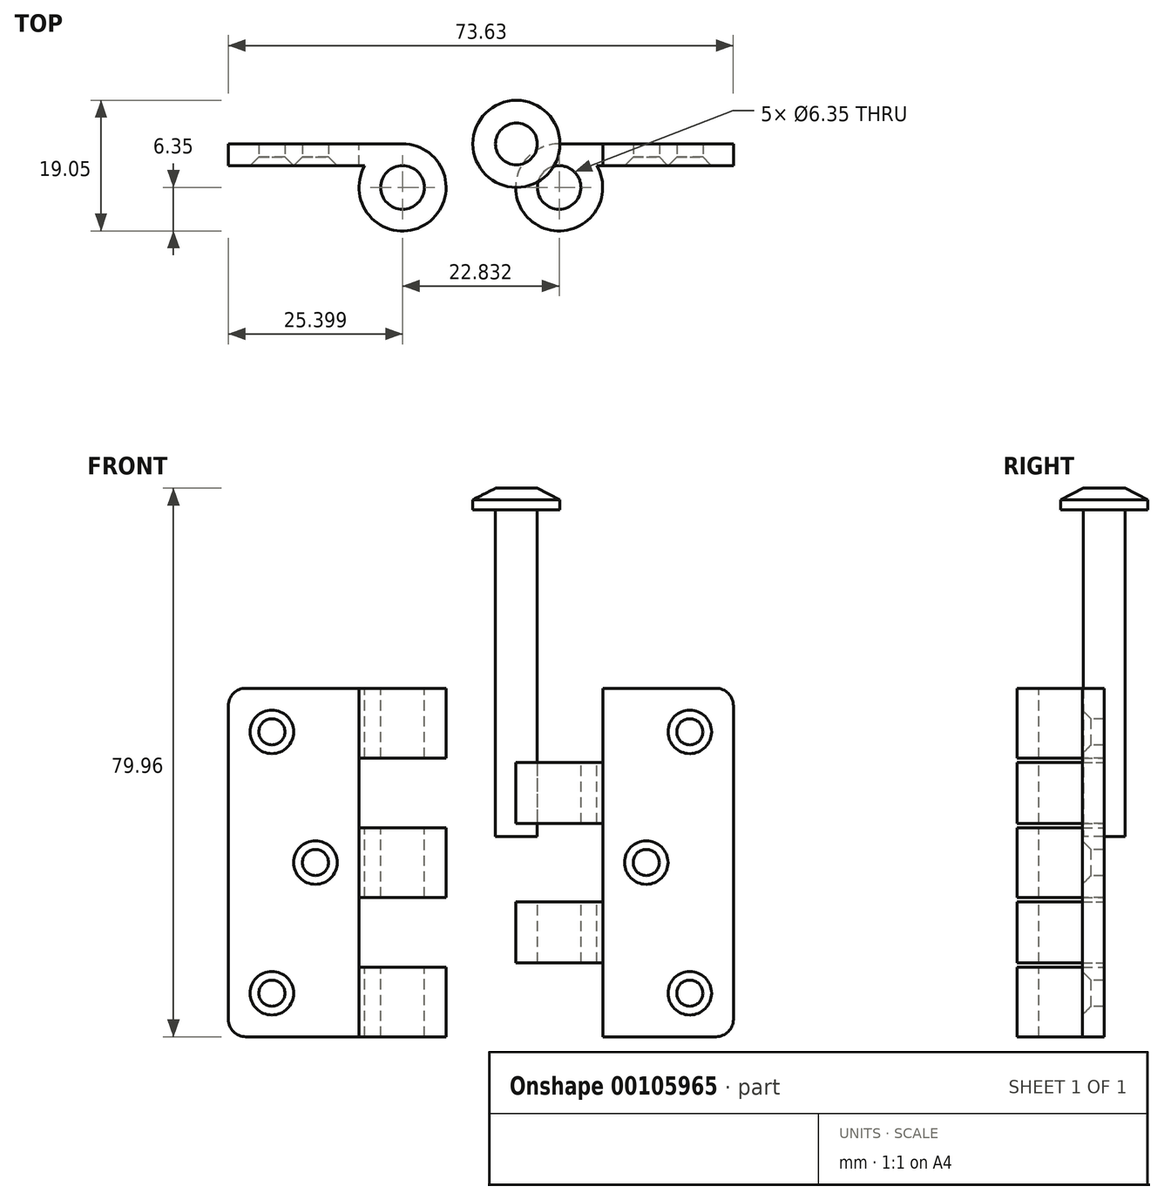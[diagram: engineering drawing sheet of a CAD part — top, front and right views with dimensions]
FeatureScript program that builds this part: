
annotation { "Feature Type Name" : "Feature", "Feature Type Description" : "" }
export const myFeature = defineFeature(function(context is Context, id is Id, definition is map)
    precondition{}
    {
        {
            var Q0;
            Q0=qCreatedBy(makeId("Front.planeOp"),FACE);
            var sketch = newSketch(context, id + "F0", { "sketchPlane" : qUnion([Q0])});
            skLineSegment(sketch, "E0.bottom", {"start": v(-44.61, 38.03) * mm, "end": v(-19.21, 38.03) * mm});
            skLineSegment(sketch, "E0.top", {"start": v(-44.61, -12.77) * mm, "end": v(-19.21, -12.77) * mm});
            skLineSegment(sketch, "E0.left", {"start": v(-44.61, 38.03) * mm, "end": v(-44.61, -12.77) * mm});
            skLineSegment(sketch, "E0.right", {"start": v(-19.21, 38.03) * mm, "end": v(-19.21, -12.77) * mm});
            skSolve(sketch);
        }
        {
            var Q0;
            Q0 = qSketchRegion(id + "F0", true);
            extrude(context, id + "F1", {"entities" : qUnion([Q0]), "depth" : 3.17 * mm});
        }
        {
            var Q0;
            Q0=makeQuery(id+"F1.opExtrude","SWEPT_FACE",FACE,{"disambiguationData":[OSD([sQuery(id+"F0.wireOp",EDGE,"E0.bottom")])]});
            var sketch = newSketch(context, id + "F2", { "sketchPlane" : qUnion([Q0])});
            skCircle(sketch, "E1", {"center": v(-19.21, -6.35) * mm, "radius": 6.35 * mm});
            skCircle(sketch, "E2", {"center": v(-19.21, -6.35) * mm, "radius": 3.18 * mm});
            skSolve(sketch);
        }
        {
            var Q0;
            {var subQ5=sQuery(id+"F2.wireOp",EDGE,"E2");Q0=makeQuery(id+"F2.imprint","IMPRINT",FACE,{"disambiguationData":[TD([[makeQuery(id+"F2.imprint","IMPRINT",EDGE,{"derivedFrom":subQ5}),-1.0]])]});}
            var Q1;
            {var subQ1=sQuery(id+"F0.wireOp",EDGE,"E0.bottom");var subQ2=makeQuery(id+"F1.opExtrude","SWEPT_EDGE",EDGE,{"disambiguationData":[OSD([subQ1,sQuery(id+"F0.wireOp",EDGE,"E0.right")])]});Q1=makeQuery(id+"F2.imprint","IMPRINT",FACE,{"disambiguationData":[TD([[makeQuery(id+"F2.imprint","IMPRINT",EDGE,{"derivedFrom":subQ2}),1.0]])]});}
            var Q2;
            Q2=makeQuery(id+"F1.opExtrude","SWEPT_FACE",FACE,{"disambiguationData":[OSD([sQuery(id+"F0.wireOp",EDGE,"E0.top")])]});
            extrude(context, id + "F3", {"entities" : qUnion([Q0, Q1]), "operationType" : NewBodyOperationType.ADD, "endBound" : BoundingType.UP_TO_SURFACE, "oppositeDirection" : true, "endBoundEntityFace" : qUnion([Q2]), "depth" : 25.4 * mm});
        }
        {
            var Q0;
            Q0=makeQuery(id+"F1.opExtrude","CAP_FACE",FACE,{"disambiguationData":[OSD([sQuery(id+"F0.wireOp",EDGE,"E0.bottom"),sQuery(id+"F0.wireOp",EDGE,"E0.top"),sQuery(id+"F0.wireOp",EDGE,"E0.left"),sQuery(id+"F0.wireOp",EDGE,"E0.right")])],"isStart":false});
            var sketch = newSketch(context, id + "F4", { "sketchPlane" : qUnion([Q0])});
            skLineSegment(sketch, "E3", {"start": v(-34.66, 38.03) * mm, "end": v(-34.66, -12.77) * mm, "construction": true});
            skLineSegment(sketch, "E4", {"start": v(-24.7, 12.63) * mm, "end": v(-44.61, 12.63) * mm, "construction": true});
            skLineSegment(sketch, "E5", {"start": v(-24.7, -6.42) * mm, "end": v(-44.61, -6.42) * mm, "construction": true});
            skLineSegment(sketch, "E6", {"start": v(-24.7, 31.68) * mm, "end": v(-44.61, 31.68) * mm, "construction": true});
            skPoint(sketch, "E7", {"position": v(-38.26, 31.68) * mm});
            skPoint(sketch, "E8", {"position": v(-31.91, 12.63) * mm});
            skPoint(sketch, "E9", {"position": v(-38.26, -6.42) * mm});
            skSolve(sketch);
        }
        {
            var Q0;
            Q0=makeQuery(id+"F1.opExtrude","SWEPT_EDGE",EDGE,{"disambiguationData":[OSD([sQuery(id+"F0.wireOp",EDGE,"E0.bottom"),sQuery(id+"F0.wireOp",EDGE,"E0.left")])]});
            var Q1;
            Q1=makeQuery(id+"F1.opExtrude","SWEPT_EDGE",EDGE,{"disambiguationData":[OSD([sQuery(id+"F0.wireOp",EDGE,"E0.top"),sQuery(id+"F0.wireOp",EDGE,"E0.left")])]});
            fillet(context, id + "F5", {"entities" : qUnion([Q0, Q1]), "radius" : 2.54 * mm, "tangentPropagation" : true, "allowEdgeOverflow" : false});
        }
        {
            var Q0;
            Q0=makeQuery(id+"F0.imprint","IMPRINT",FACE,{"disambiguationData":[TD([[makeQuery(id+"F0.imprint","IMPRINT",EDGE,{"derivedFrom":sQuery(id+"F0.wireOp",EDGE,"E0.bottom")}),-1.0]])]});
            var sketch = newSketch(context, id + "F6", { "sketchPlane" : qUnion([Q0])});
            skLineSegment(sketch, "E10", {"start": v(-25.56, -2.61) * mm, "end": v(-12.86, -2.61) * mm});
            skLineSegment(sketch, "E11", {"start": v(-12.86, -2.61) * mm, "end": v(-12.86, 7.55) * mm});
            skLineSegment(sketch, "E12", {"start": v(-12.86, 7.55) * mm, "end": v(-25.56, 7.55) * mm});
            skLineSegment(sketch, "E13", {"start": v(-25.56, 7.55) * mm, "end": v(-25.56, -2.61) * mm});
            skLineSegment(sketch, "E14", {"start": v(-25.56, 17.7) * mm, "end": v(-12.86, 17.7) * mm});
            skLineSegment(sketch, "E15", {"start": v(-12.86, 17.7) * mm, "end": v(-12.86, 27.87) * mm});
            skLineSegment(sketch, "E16", {"start": v(-12.86, 27.87) * mm, "end": v(-25.56, 27.87) * mm});
            skLineSegment(sketch, "E17", {"start": v(-25.56, 27.87) * mm, "end": v(-25.56, 17.7) * mm});
            skPoint(sketch, "E18", {"position": v(-19.21, -2.61) * mm});
            skLineSegment(sketch, "E19", {"start": v(-19.21, 27.87) * mm, "end": v(-19.21, 38.03) * mm});
            skLineSegment(sketch, "E20", {"start": v(-19.21, 17.7) * mm, "end": v(-19.21, 7.55) * mm});
            skLineSegment(sketch, "E21", {"start": v(-19.21, -2.61) * mm, "end": v(-19.21, -12.77) * mm});
            skLineSegment(sketch, "E22", {"start": v(-12.86, 17.7) * mm, "end": v(-12.86, 7.55) * mm});
            skLineSegment(sketch, "E23", {"start": v(-25.56, 7.55) * mm, "end": v(-25.56, 17.7) * mm});
            skLineSegment(sketch, "E24", {"start": v(-25.56, 27.87) * mm, "end": v(-25.56, 38.04) * mm});
            skLineSegment(sketch, "E25", {"start": v(-25.56, 38.04) * mm, "end": v(-12.86, 38.03) * mm});
            skLineSegment(sketch, "E26", {"start": v(-12.86, 38.03) * mm, "end": v(-12.86, 27.87) * mm});
            skLineSegment(sketch, "E27", {"start": v(-12.86, -2.61) * mm, "end": v(-12.86, -12.77) * mm});
            skLineSegment(sketch, "E28", {"start": v(-12.86, -12.77) * mm, "end": v(-25.56, -12.77) * mm});
            skLineSegment(sketch, "E29", {"start": v(-25.56, -12.77) * mm, "end": v(-25.56, -2.61) * mm});
            skSolve(sketch);
        }
        {
            var Q0;
            {var subQ0=sQuery(id+"F6.wireOp",EDGE,"E17");Q0=makeQuery(id+"F6.imprint","IMPRINT",FACE,{"disambiguationData":[TD([[makeQuery(id+"F6.imprint","IMPRINT",EDGE,{"derivedFrom":subQ0}),1.0]])]});}
            var Q1;
            {var subQ0=sQuery(id+"F6.wireOp",EDGE,"E15");Q1=makeQuery(id+"F6.imprint","IMPRINT",FACE,{"disambiguationData":[TD([[makeQuery(id+"F6.imprint","IMPRINT",EDGE,{"derivedFrom":subQ0}),1.0]])]});}
            var Q2;
            {var subQ0=sQuery(id+"F6.wireOp",EDGE,"E13");Q2=makeQuery(id+"F6.imprint","IMPRINT",FACE,{"disambiguationData":[TD([[makeQuery(id+"F6.imprint","IMPRINT",EDGE,{"derivedFrom":subQ0}),1.0]])]});}
            var Q3;
            {var subQ0=sQuery(id+"F6.wireOp",EDGE,"E11");Q3=makeQuery(id+"F6.imprint","IMPRINT",FACE,{"disambiguationData":[TD([[makeQuery(id+"F6.imprint","IMPRINT",EDGE,{"derivedFrom":subQ0}),1.0]])]});}
            extrude(context, id + "F7", {"entities" : qUnion([Q0, Q1, Q2, Q3]), "operationType" : NewBodyOperationType.REMOVE, "depth" : 25.4 * mm});
        }
        {
            var Q0;
            Q0=qCreatedBy(makeId("Front.planeOp"),FACE);
            var sketch = newSketch(context, id + "F8", { "sketchPlane" : qUnion([Q0])});
            skLineSegment(sketch, "E30.bottom", {"start": v(3.62, 38.03) * mm, "end": v(29.02, 38.03) * mm});
            skLineSegment(sketch, "E30.top", {"start": v(3.62, -12.77) * mm, "end": v(29.02, -12.77) * mm});
            skLineSegment(sketch, "E30.left", {"start": v(3.62, 38.03) * mm, "end": v(3.62, -12.77) * mm});
            skLineSegment(sketch, "E30.right", {"start": v(29.02, 38.03) * mm, "end": v(29.02, -12.77) * mm});
            skSolve(sketch);
        }
        {
            var Q0;
            Q0 = qSketchRegion(id + "F8", true);
            extrude(context, id + "F9", {"entities" : qUnion([Q0]), "depth" : 3.17 * mm});
        }
        {
            var Q0;
            Q0=makeQuery(id+"F9.opExtrude","SWEPT_FACE",FACE,{"disambiguationData":[OSD([sQuery(id+"F8.wireOp",EDGE,"E30.bottom")])]});
            var sketch = newSketch(context, id + "F10", { "sketchPlane" : qUnion([Q0])});
            skCircle(sketch, "E31", {"center": v(3.62, -6.35) * mm, "radius": 6.35 * mm});
            skLineSegment(sketch, "E32", {"start": v(-33.9, -6.35) * mm, "end": v(23.07, -6.35) * mm, "construction": true});
            skCircle(sketch, "E33", {"center": v(3.62, -6.35) * mm, "radius": 3.18 * mm});
            skSolve(sketch);
        }
        {
            var Q0;
            {var subQ5=sQuery(id+"F10.wireOp",EDGE,"E33");Q0=makeQuery(id+"F10.imprint","IMPRINT",FACE,{"disambiguationData":[TD([[makeQuery(id+"F10.imprint","IMPRINT",EDGE,{"derivedFrom":subQ5}),-1.0]])]});}
            var Q1;
            {var subQ1=sQuery(id+"F8.wireOp",EDGE,"E30.bottom");var subQ2=makeQuery(id+"F9.opExtrude","SWEPT_EDGE",EDGE,{"disambiguationData":[OSD([subQ1,sQuery(id+"F8.wireOp",EDGE,"E30.left")])]});Q1=makeQuery(id+"F10.imprint","IMPRINT",FACE,{"disambiguationData":[TD([[makeQuery(id+"F10.imprint","IMPRINT",EDGE,{"derivedFrom":subQ2}),-1.0]])]});}
            var Q2;
            Q2=makeQuery(id+"F9.opExtrude","SWEPT_FACE",FACE,{"disambiguationData":[OSD([sQuery(id+"F8.wireOp",EDGE,"E30.top")])]});
            extrude(context, id + "F11", {"entities" : qUnion([Q0, Q1]), "operationType" : NewBodyOperationType.ADD, "endBound" : BoundingType.UP_TO_SURFACE, "oppositeDirection" : true, "endBoundEntityFace" : qUnion([Q2]), "depth" : 25.4 * mm});
        }
        {
            var Q0;
            Q0=makeQuery(id+"F9.opExtrude","CAP_FACE",FACE,{"disambiguationData":[OSD([sQuery(id+"F8.wireOp",EDGE,"E30.bottom"),sQuery(id+"F8.wireOp",EDGE,"E30.top"),sQuery(id+"F8.wireOp",EDGE,"E30.left"),sQuery(id+"F8.wireOp",EDGE,"E30.right")])],"isStart":true});
            var sketch = newSketch(context, id + "F12", { "sketchPlane" : qUnion([Q0])});
            skLineSegment(sketch, "E34", {"start": v(-9.97, 27.23) * mm, "end": v(2.73, 27.23) * mm});
            skLineSegment(sketch, "E35", {"start": v(2.73, 27.23) * mm, "end": v(2.73, 38.03) * mm});
            skLineSegment(sketch, "E36", {"start": v(2.73, 38.03) * mm, "end": v(-9.97, 38.03) * mm});
            skLineSegment(sketch, "E37", {"start": v(-9.97, 27.23) * mm, "end": v(-9.97, 38.03) * mm});
            skLineSegment(sketch, "E38", {"start": v(-9.97, 27.23) * mm, "end": v(-9.97, -12.77) * mm});
            skLineSegment(sketch, "E39", {"start": v(-9.97, -12.77) * mm, "end": v(2.73, -12.77) * mm});
            skLineSegment(sketch, "E40", {"start": v(2.73, -12.77) * mm, "end": v(2.73, 27.23) * mm});
            skLineSegment(sketch, "E41", {"start": v(2.73, 18.34) * mm, "end": v(-9.97, 18.34) * mm});
            skLineSegment(sketch, "E42", {"start": v(-9.97, 6.91) * mm, "end": v(2.73, 6.91) * mm});
            skLineSegment(sketch, "E43", {"start": v(-9.97, -1.98) * mm, "end": v(2.73, -1.98) * mm});
            skSolve(sketch);
        }
        {
            var Q0;
            {var subQ0=sQuery(id+"F12.wireOp",EDGE,"E35");Q0=makeQuery(id+"F12.imprint","IMPRINT",FACE,{"disambiguationData":[TD([[makeQuery(id+"F12.imprint","IMPRINT",EDGE,{"derivedFrom":subQ0}),1.0]])]});}
            var Q1;
            {var subQ0=sQuery(id+"F12.wireOp",EDGE,"E37");Q1=makeQuery(id+"F12.imprint","IMPRINT",FACE,{"disambiguationData":[TD([[makeQuery(id+"F12.imprint","IMPRINT",EDGE,{"derivedFrom":subQ0}),-1.0]])]});}
            var Q2;
            {var subQ0=sQuery(id+"F12.wireOp",EDGE,"E41");var subQ1=sQuery(id+"F12.wireOp",EDGE,"E38");var subQ2=makeQuery(id+"F12.imprint","INTERSECT",VERTEX,{"derivedFrom":[subQ1,subQ0]});Q2=makeQuery(id+"F12.imprint","IMPRINT",FACE,{"disambiguationData":[TD([[makeQuery(id+"F12.imprint","IMPRINT",EDGE,{"disambiguationData":[TD([[subQ2,-1.0]])],"derivedFrom":subQ1}),1.0]])]});}
            var Q3;
            {var subQ0=sQuery(id+"F12.wireOp",EDGE,"E41");var subQ1=sQuery(id+"F12.wireOp",EDGE,"E40");var subQ2=makeQuery(id+"F12.imprint","INTERSECT",VERTEX,{"derivedFrom":[subQ1,subQ0]});Q3=makeQuery(id+"F12.imprint","IMPRINT",FACE,{"disambiguationData":[TD([[makeQuery(id+"F12.imprint","IMPRINT",EDGE,{"disambiguationData":[TD([[subQ2,1.0]])],"derivedFrom":subQ1}),1.0]])]});}
            var Q4;
            {var subQ0=sQuery(id+"F12.wireOp",EDGE,"E39");var subQ3=sQuery(id+"F12.wireOp",EDGE,"E40");var subQ4=makeQuery(id+"F12.imprint","INTERSECT",VERTEX,{"derivedFrom":[subQ0,subQ3]});Q4=makeQuery(id+"F12.imprint","IMPRINT",FACE,{"disambiguationData":[TD([[makeQuery(id+"F12.imprint","IMPRINT",EDGE,{"disambiguationData":[TD([[subQ4,1.0]])],"derivedFrom":subQ0}),1.0]])]});}
            var Q5;
            {var subQ1=sQuery(id+"F12.wireOp",EDGE,"E38");var subQ3=sQuery(id+"F12.wireOp",EDGE,"E43");var subQ4=makeQuery(id+"F12.imprint","INTERSECT",VERTEX,{"derivedFrom":[subQ1,subQ3]});Q5=makeQuery(id+"F12.imprint","IMPRINT",FACE,{"disambiguationData":[TD([[makeQuery(id+"F12.imprint","IMPRINT",EDGE,{"disambiguationData":[TD([[subQ4,-1.0]])],"derivedFrom":subQ3}),-1.0]])]});}
            extrude(context, id + "F13", {"entities" : qUnion([Q0, Q1, Q2, Q3, Q4, Q5]), "operationType" : NewBodyOperationType.REMOVE, "oppositeDirection" : true, "depth" : 25.4 * mm});
        }
        {
            var Q0;
            Q0=qCreatedBy(makeId("Front.planeOp"),FACE);
            var sketch = newSketch(context, id + "F14", { "sketchPlane" : qUnion([Q0])});
            skLineSegment(sketch, "E44", {"start": v(-5.65, 64.02) * mm, "end": v(-5.65, 16.4) * mm});
            skLineSegment(sketch, "E45", {"start": v(-5.65, 16.4) * mm, "end": v(-2.6, 16.4) * mm});
            skLineSegment(sketch, "E46", {"start": v(-2.6, 16.4) * mm, "end": v(-2.6, 67.2) * mm});
            skLineSegment(sketch, "E47", {"start": v(-2.6, 67.2) * mm, "end": v(-5.65, 67.2) * mm});
            skLineSegment(sketch, "E48", {"start": v(-5.65, 67.2) * mm, "end": v(-8.96, 65.52) * mm});
            skLineSegment(sketch, "E49", {"start": v(-8.96, 65.52) * mm, "end": v(-8.96, 64.02) * mm});
            skLineSegment(sketch, "E50", {"start": v(-8.96, 64.02) * mm, "end": v(-5.65, 64.02) * mm});
            skSolve(sketch);
        }
        {
            var Q0;
            Q0 = qSketchRegion(id + "F14", true);
            var Q1;
            Q1=sQuery(id+"F14.wireOp",EDGE,"E46");
            revolve(context, id + "F15", {"entities" : qUnion([Q0]), "axis" : qUnion([Q1]), "revolveType" : RevolveType.FULL});
        }
        {
            var Q0;
            Q0=makeQuery(id+"F9.opExtrude","CAP_FACE",FACE,{"disambiguationData":[OSD([sQuery(id+"F8.wireOp",EDGE,"E30.bottom"),sQuery(id+"F8.wireOp",EDGE,"E30.top"),sQuery(id+"F8.wireOp",EDGE,"E30.left"),sQuery(id+"F8.wireOp",EDGE,"E30.right")])],"isStart":false});
            var sketch = newSketch(context, id + "F16", { "sketchPlane" : qUnion([Q0])});
            skLineSegment(sketch, "E51", {"start": v(19.5, 38.03) * mm, "end": v(19.5, -12.77) * mm, "construction": true});
            skLineSegment(sketch, "E52", {"start": v(9.97, 12.63) * mm, "end": v(29.02, 12.63) * mm, "construction": true});
            skPoint(sketch, "E53", {"position": v(16.32, 12.63) * mm});
            skPoint(sketch, "E54", {"position": v(22.67, 31.68) * mm});
            skPoint(sketch, "E55", {"position": v(22.67, -6.42) * mm});
            skSolve(sketch);
        }
        {
            var Q0;
            Q0=sQuery(id+"F4.wireOp",VERTEX,"E7");
            var Q1;
            Q1=sQuery(id+"F4.wireOp",VERTEX,"E8");
            var Q2;
            Q2=sQuery(id+"F4.wireOp",VERTEX,"E9");
            var Q3;
            Q3=makeQuery(id+"F1.opExtrude","SWEPT_BODY",BODY,{"disambiguationData":[OSD([sQuery(id+"F0.wireOp",EDGE,"E0.bottom"),sQuery(id+"F0.wireOp",EDGE,"E0.top"),sQuery(id+"F0.wireOp",EDGE,"E0.left"),sQuery(id+"F0.wireOp",EDGE,"E0.right")])]});
            hole(context, id + "F17", {"style" : HoleStyle.C_SINK, "endStyle" : HoleEndStyle.THROUGH, "holeDiameter" : 3.8 * mm, "cSinkDiameter" : 6.35 * mm, "cSinkAngle" : 90 * degree, "locations" : qUnion([Q0, Q1, Q2]), "scope" : qUnion([Q3]), "isTappedThrough" : true});
        }
        {
            var Q0;
            Q0=sQuery(id+"F16.wireOp",VERTEX,"E54");
            var Q1;
            Q1=sQuery(id+"F16.wireOp",VERTEX,"E53");
            var Q2;
            Q2=sQuery(id+"F16.wireOp",VERTEX,"E55");
            var Q3;
            Q3=makeQuery(id+"F9.opExtrude","SWEPT_BODY",BODY,{"disambiguationData":[OSD([sQuery(id+"F8.wireOp",EDGE,"E30.bottom"),sQuery(id+"F8.wireOp",EDGE,"E30.top"),sQuery(id+"F8.wireOp",EDGE,"E30.left"),sQuery(id+"F8.wireOp",EDGE,"E30.right")])]});
            hole(context, id + "F18", {"style" : HoleStyle.C_SINK, "endStyle" : HoleEndStyle.THROUGH, "holeDiameter" : 3.8 * mm, "cSinkDiameter" : 6.35 * mm, "cSinkAngle" : 90 * degree, "locations" : qUnion([Q0, Q1, Q2]), "scope" : qUnion([Q3]), "isTappedThrough" : true});
        }
        {
            var Q0;
            Q0=makeQuery(id+"F9.opExtrude","SWEPT_EDGE",EDGE,{"disambiguationData":[OSD([sQuery(id+"F8.wireOp",EDGE,"E30.bottom"),sQuery(id+"F8.wireOp",EDGE,"E30.right")])]});
            var Q1;
            Q1=makeQuery(id+"F9.opExtrude","SWEPT_EDGE",EDGE,{"disambiguationData":[OSD([sQuery(id+"F8.wireOp",EDGE,"E30.top"),sQuery(id+"F8.wireOp",EDGE,"E30.right")])]});
            fillet(context, id + "F19", {"entities" : qUnion([Q0, Q1]), "radius" : 2.54 * mm, "tangentPropagation" : true, "allowEdgeOverflow" : false});
        }
    });
